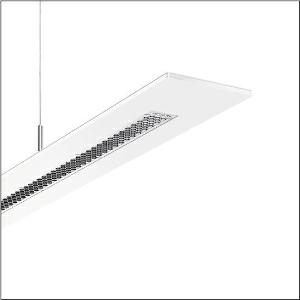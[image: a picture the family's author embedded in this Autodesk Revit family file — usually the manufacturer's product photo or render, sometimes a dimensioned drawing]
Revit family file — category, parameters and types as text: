
# Revit family: arktika_r__21_5mb2512l30840_559e
name_source: partatom
category: Lighting Fixtures
units: mm (PartAtom-declared; Revit-internal decimal feet)

## family parameters
Cut with Voids When Loaded = No
Host = Face
Light Source = No
Part Type = Normal
Room Calculation Point = No
Round Connector Dimension = Use Diameter
Shared = No

## types (1)
- Arktika® 21 (1 x LED 4000K / CRI = 80 (unbekannt), 4000 lm, 4000K)
    Apparent Load = 31 VA
    CIE Flux Codes = 81 100 100 79 100
    Color Rendering = 80
    Color Temperature = 4000K
    Default Elevation = 1800 mm
    Description = Arktika® 21, office luminaire, primary anti-glare with honeycomb louvre, of plastic, aluminium vaporised, highly specular, light emission: direct/indirect distribution, primary light characteristic: symmetric, installation type: suspended mounting, LED, rated luminous flux: 4.000lm, luminous efficacy: 130lm/W, light colour: 840, colour temperature: 4000K, control gear: ECG, with terminal, 3-pole, mains connection: 220..240V, AC, 50/60Hz, rated input power: 31W, housing, of aluminium, powder-coated, traffic white (RAL 9016), 1-length, length: 1.250mm, width: 120mm, height: 8mm, protection rating (complete): IP20, insulation class (complete): insulation class II (safety insulation), certification: CE, packaging unit: 1 piece
    Height = 8 mm  [stored 0.0262467 ft]
    Lamp = 1 x LED 4000K / CRI >= 80 (unbekannt)
    Lamp Light Flux = 4000 lm
    Lamp count = 1
    Length = 1250 mm
    Luminous efficacy = 130 lm/W
    Manufacturer = Siteco
    ModVariant = No
    Model = 5MB2512L30840
    Mounting Place = Ceiling
    Mounting Type = Pendant
    Number of Poles = 1
    OnlyDefault = Yes
    Power Factor = 1
    Product Name = Arktika® 21
    Product group = office luminaire | ceiling pendant
    ProductGroupID = 902
    Protection Class = Protection class II
    Protection Degree = IP 20
    RLX_Detail_Level = 1
    RLX_Emergency_Light_Flux = 0 lm
    RLX_Emergency_Type = 0
    RLX_Emergency_Type_DB = No
    RlxData = <blob elided: 36049 chars, md5=0b905443>
    Socket = socket
    Standby Power = 0 W
    System Light Flux = 4000 lm
    System Power = 31 W
    Type Comments = Product without accessories
    Type Image = l_1006128.jpg
    URL = http://relux.com
    VarID = ---
    Voltage = 0 V
    Weight = 0.00 kg
    Width = 120 mm

note: [stored X ft] marks values corroborated as IEEE doubles in the binary element streams (Revit-internal decimal feet)

## geometry (parser evidence)
native form markers: Blend x4, Sweep x11
no freeform markers — native parametric forms only
